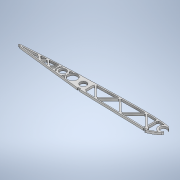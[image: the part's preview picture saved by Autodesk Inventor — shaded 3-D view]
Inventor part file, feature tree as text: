
AUTODESK INVENTOR PART (.ipt)
format: ipt  version: 2022 (Build 260153000, 153)  size: 451,584 bytes
history: native  units: mm
features: extrude x1, sketch x1
ambient origin geometry x8: Origin, YZ Plane, XZ Plane, XY Plane, X Axis, Y Axis, Z Axis, Center Point
bodies: Body1 (feature_tree)
feature tree (2):
  extrude  "Extrusion5"  Depth=10.0mm
  sketch  "Sketch1"  dims[d31=34.456mm d50=368.759386mm d57=16.0mm d69=8.0mm d70=23.0mm d71=8.0mm d73=16.0mm d80=19.0mm d81=16.0mm d82=1.0mm d83=1.0mm d84=1.0mm d85=1.0mm d86=1.0mm d87=0.8mm d88=1.0mm d90=19.0mm d94=5.0mm d95=5.0mm d105=5.0mm d106=5.0mm d108=2.0mm d109=19.0mm d114=5.0mm d115=5.0mm d116=24.0mm d117=2.5mm d118=2.5mm d123=2.5mm d124=2.5mm d125=10.0mm d126=24.0mm d127=24.0mm d128=27.0mm d135=0.5mm d136=45.0deg d139=7.0mm d165=45.0deg d169=27.0mm d175=90.0deg d181=45.0deg d185=7.0mm d186=45.0deg d190=7.0mm d191=45.0deg d197=90.0deg d203=90.0deg d206=7.0mm d207=5.0mm d208=0.0mm]
